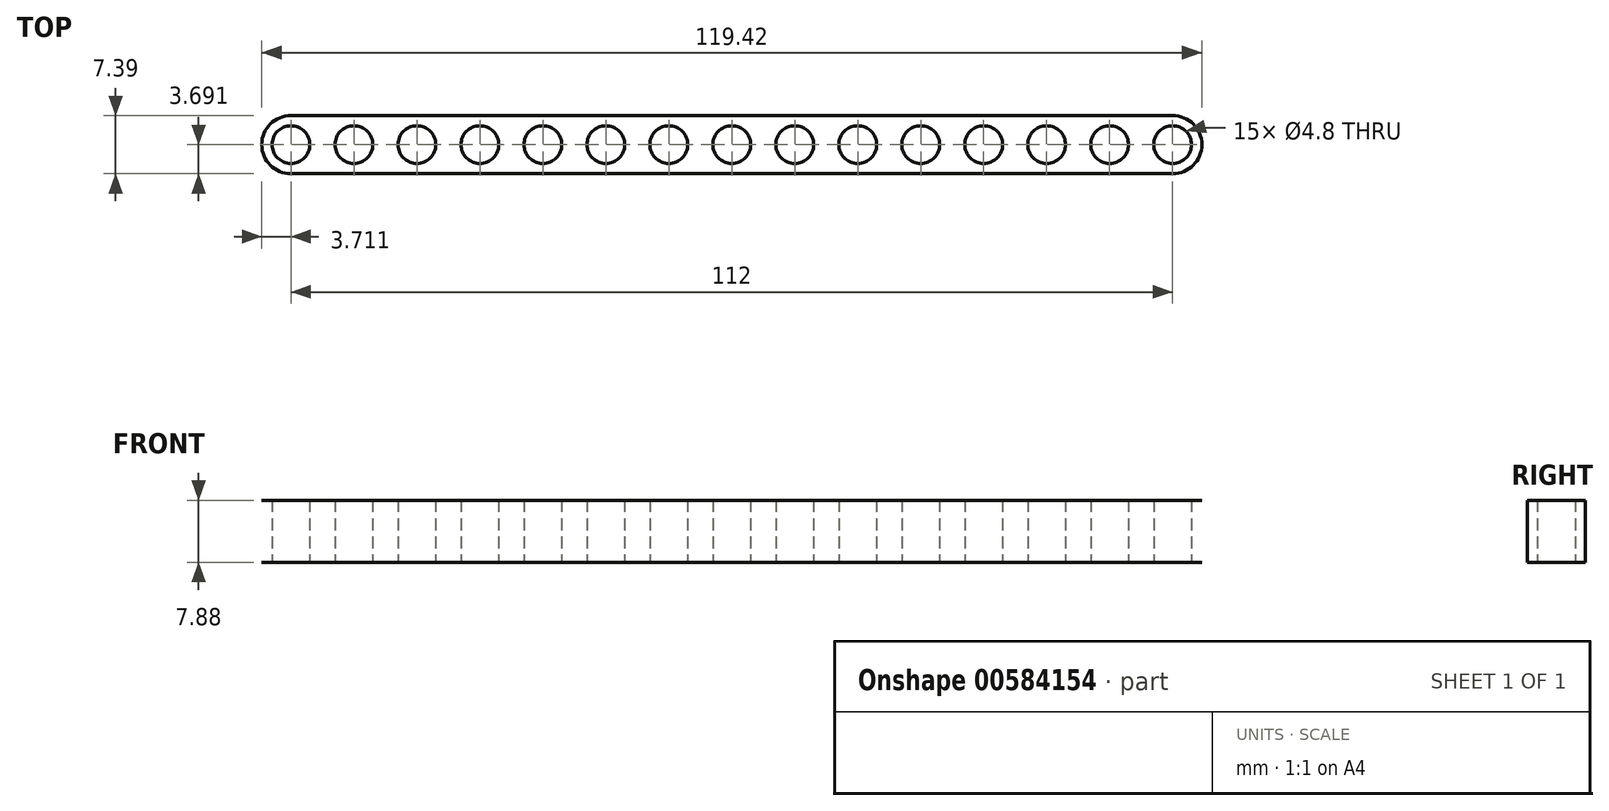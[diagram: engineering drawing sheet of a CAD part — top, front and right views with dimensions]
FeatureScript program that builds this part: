
annotation { "Feature Type Name" : "Feature", "Feature Type Description" : "" }
export const myFeature = defineFeature(function(context is Context, id is Id, definition is map)
    precondition{}
    {
        {
            var Q0;
            Q0=qCreatedBy(makeId("Top.planeOp"),FACE);
            var sketch = newSketch(context, id + "F0", { "sketchPlane" : qUnion([Q0])});
            skLineSegment(sketch, "E0", {"start": v(-28.72, 9.1) * mm, "end": v(-28.72, -19.18) * mm, "construction": true});
            skLineSegment(sketch, "E1", {"start": v(-28.72, -19.18) * mm, "end": v(-29.11, -19.18) * mm, "construction": true});
            skLineSegment(sketch, "E2", {"start": v(-1.18, -2.09) * mm, "end": v(-47.58, -2.09) * mm, "construction": true});
            skLineSegment(sketch, "E3", {"start": v(-47.58, -2.09) * mm, "end": v(-47.58, -1.54) * mm, "construction": true});
            skLineSegment(sketch, "E4", {"start": v(-28.72, 1.6) * mm, "end": v(-88.43, 1.6) * mm});
            skLineSegment(sketch, "E5", {"start": v(-88.43, 1.6) * mm, "end": v(-88.43, -2.09) * mm});
            skArc(sketch, "E6", {"start": v(-28.72, 0.31) * mm, "mid": v(-31.12, -2.09) * mm, "end": v(-28.72, -4.49) * mm});
            skCircle(sketch, "E7", {"center": v(-36.72, -2.09) * mm, "radius": 2.4 * mm});
            skCircle(sketch, "E8.1.0.0", {"center": v(-44.72, -2.09) * mm, "radius": 2.4 * mm});
            skLineSegment(sketch, "E8.direction1", {"start": v(-36.72, -2.09) * mm, "end": v(-44.72, -2.09) * mm, "construction": true});
            skCircle(sketch, "E9.0.2.0", {"center": v(-52.72, -2.09) * mm, "radius": 2.4 * mm});
            skCircle(sketch, "E9.0.3.0", {"center": v(-60.72, -2.09) * mm, "radius": 2.4 * mm});
            skCircle(sketch, "E9.0.4.0", {"center": v(-68.72, -2.09) * mm, "radius": 2.4 * mm});
            skLineSegment(sketch, "E10.MirrorCS", {"start": v(-28.72, -5.78) * mm, "end": v(-88.43, -5.78) * mm});
            skLineSegment(sketch, "E11.MirrorCS", {"start": v(-88.43, -5.78) * mm, "end": v(-88.43, -2.09) * mm});
            skLineSegment(sketch, "E12.MirrorCS", {"start": v(-9.86, -2.09) * mm, "end": v(-9.86, -1.54) * mm, "construction": true});
            skLineSegment(sketch, "E13.MirrorCS", {"start": v(-56.26, -2.09) * mm, "end": v(-9.86, -2.09) * mm, "construction": true});
            skArc(sketch, "E14.MirrorCS", {"start": v(-28.72, 0.31) * mm, "mid": v(-26.32, -2.09) * mm, "end": v(-28.72, -4.49) * mm});
            skCircle(sketch, "E15.MirrorC", {"center": v(-20.72, -2.09) * mm, "radius": 2.4 * mm});
            skCircle(sketch, "E16.MirrorC", {"center": v(-12.72, -2.09) * mm, "radius": 2.4 * mm});
            skLineSegment(sketch, "E17.MirrorCS", {"start": v(-28.72, 1.6) * mm, "end": v(31, 1.6) * mm});
            skLineSegment(sketch, "E18.MirrorCS", {"start": v(31, 1.6) * mm, "end": v(31, -2.09) * mm});
            skLineSegment(sketch, "E19.MirrorCS", {"start": v(31, -5.78) * mm, "end": v(31, -2.09) * mm});
            skLineSegment(sketch, "E20.MirrorCS", {"start": v(-28.72, -5.78) * mm, "end": v(31, -5.78) * mm});
            skCircle(sketch, "E21.MirrorC", {"center": v(-4.72, -2.09) * mm, "radius": 2.4 * mm});
            skLineSegment(sketch, "E22.MirrorCS", {"start": v(-20.72, -2.09) * mm, "end": v(-12.72, -2.09) * mm, "construction": true});
            skCircle(sketch, "E23.MirrorC", {"center": v(11.28, -2.09) * mm, "radius": 2.4 * mm});
            skCircle(sketch, "E24.MirrorC", {"center": v(3.28, -2.09) * mm, "radius": 2.4 * mm});
            skCircle(sketch, "E25.0.5.0", {"center": v(-76.72, -2.09) * mm, "radius": 2.4 * mm});
            skCircle(sketch, "E25.0.6.0", {"center": v(-84.72, -2.09) * mm, "radius": 2.4 * mm});
            skCircle(sketch, "E26.MirrorC", {"center": v(19.28, -2.09) * mm, "radius": 2.4 * mm});
            skCircle(sketch, "E27.MirrorC", {"center": v(27.28, -2.09) * mm, "radius": 2.4 * mm});
            skSolve(sketch);
        }
        {
            var Q0;
            Q0=makeQuery(id+"F0.imprint","IMPRINT",FACE,{"disambiguationData":[TD([[makeQuery(id+"F0.imprint","IMPRINT",EDGE,{"derivedFrom":sQuery(id+"F0.wireOp",EDGE,"E4")}),1.0]])]});
            extrude(context, id + "F1", {"entities" : qUnion([Q0]), "depth" : 7.88 * mm, "offsetDistance" : 25 * mm});
        }
        {
            var Q0;
            Q0=makeQuery(id+"F1.opExtrude","SWEPT_EDGE",EDGE,{"disambiguationData":[OSD([sQuery(id+"F0.wireOp",EDGE,"E17.MirrorCS"),sQuery(id+"F0.wireOp",EDGE,"E18.MirrorCS")])]});
            var Q1;
            Q1=makeQuery(id+"F1.opExtrude","SWEPT_EDGE",EDGE,{"disambiguationData":[OSD([sQuery(id+"F0.wireOp",EDGE,"E19.MirrorCS"),sQuery(id+"F0.wireOp",EDGE,"E20.MirrorCS")])]});
            var Q2;
            Q2=makeQuery(id+"F1.opExtrude","SWEPT_EDGE",EDGE,{"disambiguationData":[OSD([sQuery(id+"F0.wireOp",EDGE,"E4"),sQuery(id+"F0.wireOp",EDGE,"E5")])]});
            var Q3;
            Q3=makeQuery(id+"F1.opExtrude","SWEPT_EDGE",EDGE,{"disambiguationData":[OSD([sQuery(id+"F0.wireOp",EDGE,"E10.MirrorCS"),sQuery(id+"F0.wireOp",EDGE,"E11.MirrorCS")])]});
            fillet(context, id + "F2", {"entities" : qUnion([Q0, Q1, Q2, Q3]), "radius" : 3.7 * mm, "tangentPropagation" : true, "allowEdgeOverflow" : false});
        }
    });
